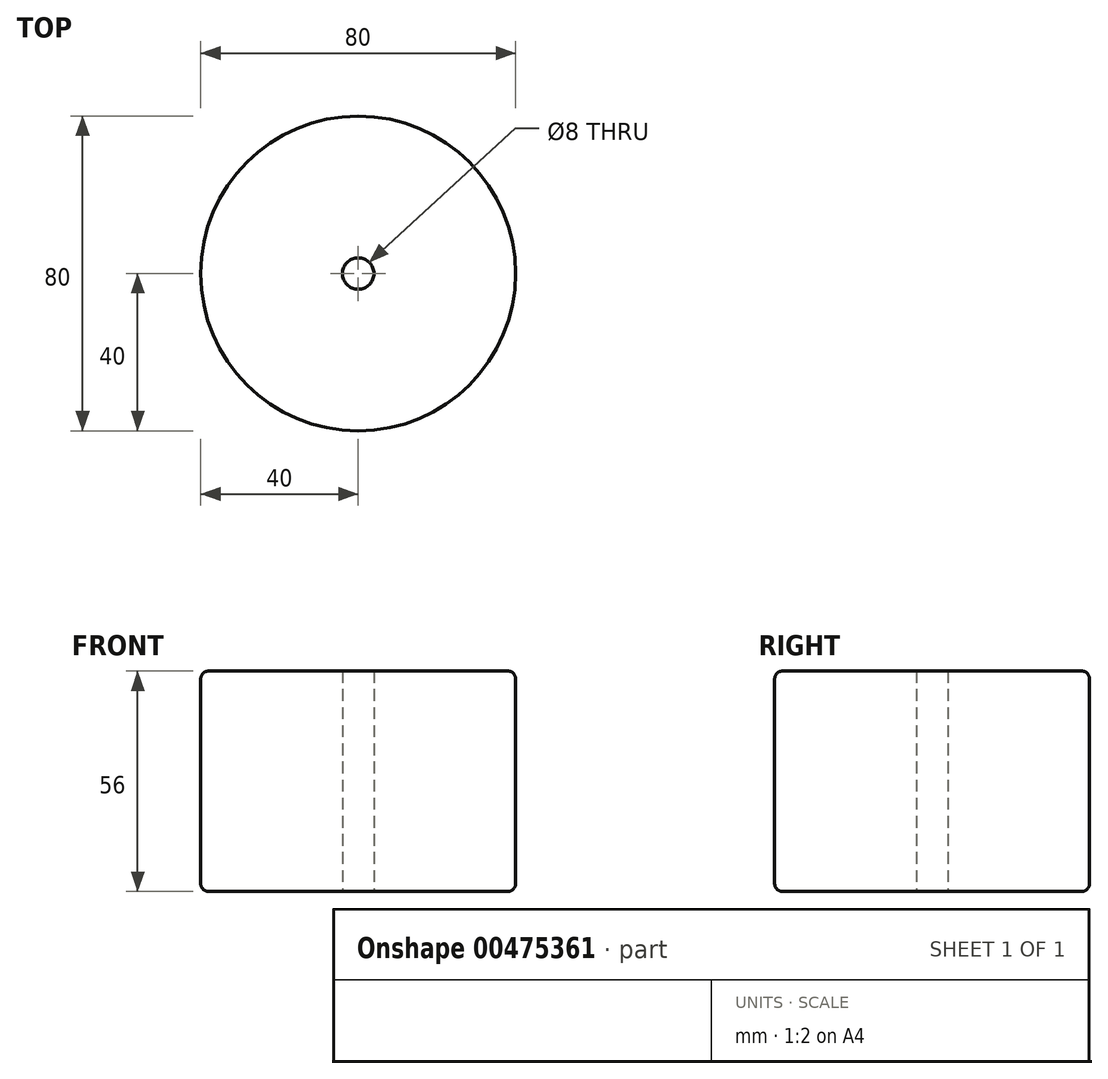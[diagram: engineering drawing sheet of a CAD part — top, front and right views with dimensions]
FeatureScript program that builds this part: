
annotation { "Feature Type Name" : "Feature", "Feature Type Description" : "" }
export const myFeature = defineFeature(function(context is Context, id is Id, definition is map)
    precondition{}
    {
        {
            var Q0;
            Q0=qCreatedBy(makeId("Top.planeOp"),FACE);
            var sketch = newSketch(context, id + "F0", { "sketchPlane" : qUnion([Q0])});
            skCircle(sketch, "E0", {"center": v(0, 0) * mm, "radius": 40 * mm});
            skSolve(sketch);
        }
        {
            var Q0;
            Q0=makeQuery(id+"F0.imprint","IMPRINT",FACE,{"disambiguationData":[TD([[makeQuery(id+"F0.imprint","IMPRINT",EDGE,{"derivedFrom":sQuery(id+"F0.wireOp",EDGE,"E0")}),1.0]])]});
            extrude(context, id + "F1", {"entities" : qUnion([Q0]), "depth" : 56 * mm});
        }
        {
            var Q0;
            Q0=sQuery(id+"F0.wireOp",VERTEX,"E0.center");
            var Q1;
            Q1=makeQuery(id+"F1.opExtrude","SWEPT_BODY",BODY,{"disambiguationData":[OSD([sQuery(id+"F0.wireOp",EDGE,"E0")])]});
            hole(context, id + "F2", {"style" : HoleStyle.SIMPLE, "endStyle" : HoleEndStyle.THROUGH, "oppositeDirection" : true, "standardTappedOrClearance" : lookupTablePath({ "standard" : "ISO", "size" : "8", "type" : "Drilled" }), "standardBlindInLast" : lookupTablePath({ "standard" : "ISO", "size" : "8", "type" : "Drilled" }), "holeDiameter" : 8 * mm, "isTappedThrough" : true, "tappedDepth" : 12 * mm, "tapClearance" : 3, "locations" : qUnion([Q0]), "scope" : qUnion([Q1])});
        }
        {
            var Q0;
            Q0=makeQuery(id+"F1.opExtrude","SWEPT_FACE",FACE,{"disambiguationData":[OSD([sQuery(id+"F0.wireOp",EDGE,"E0")])]});
            var Q1;
            Q1=makeQuery(id+"F1.opExtrude","CAP_EDGE",EDGE,{"disambiguationData":[OSD([sQuery(id+"F0.wireOp",EDGE,"E0")])],"isStart":false});
            fillet(context, id + "F3", {"entities" : qUnion([Q0, Q1]), "radius" : 2 * mm, "tangentPropagation" : true, "allowEdgeOverflow" : false});
        }
    });
